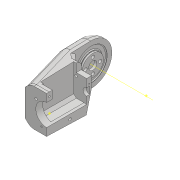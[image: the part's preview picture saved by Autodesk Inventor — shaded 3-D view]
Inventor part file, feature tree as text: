
AUTODESK INVENTOR PART (.ipt)
format: ipt  version: 2018 (Build 220112000, 112)  size: 1,027,584 bytes
history: native  units: mm
features: projected_geometry x49, sketch x47, extrude x39, hole x13, fillet x12, other x10, chamfer x6, reference x3, mirror x1, plane x1
ambient origin geometry x8: Origin, YZ Plane, XZ Plane, XY Plane, X Axis, Y Axis, Z Axis, Center Point
bodies: Solid1 (feature_tree)
feature tree (181):
  extrude  "Extrusion1"  Depth=45.0mm
  extrude  "Extrusion2"  Depth=2.25mm
  hole  "Hole1"  [1 undecoded]
  hole  "Hole2"  [1 undecoded]
  fillet  "Fillet1"  Radius=14.0mm
  extrude  "Extrusion3"  Depth=18.5mm
  extrude  "Extrusion4"  Depth=10.0mm
  extrude  "Extrusion5"  Depth=2.0mm
  extrude  "Extrusion6"  Depth=8.0mm
  hole  "Hole3"  [1 undecoded]
  extrude  "Extrusion7"  Depth=0.5mm
  extrude  "Extrusion8"  Depth=1.0mm TaperAngle=0.0deg
  extrude  "Extrusion9"  Depth=24.5mm
  extrude  "Extrusion10"  Depth=10.0mm
  extrude  "Extrusion11"  Depth=14.5mm
  extrude  "Extrusion13"  Depth=14.5mm
  extrude  "Extrusion14"  Depth=5.0mm
  extrude  "Extrusion15"  Depth=2.25mm
  extrude  "Extrusion16"  Depth=5.0mm
  extrude  "Extrusion17"  Depth=9.0mm
  chamfer  "Chamfer1"  Distance=1.0mm
  fillet  "Fillet7"  Radius=20.7mm
  fillet  "Fillet8"  Radius=32.0mm
  mirror  "Mirror1"
  sketch  "Sketch26"  dims[d55=2.25mm d56=5.0mm]
  extrude  "Extrusion24"  Depth=1.0mm TaperAngle=0.0deg
  extrude  "Extrusion25"  Depth=8.0mm
  extrude  "Extrusion26"  Depth=0.2mm TaperAngle=0.0deg
  extrude  "Extrusion27"  Depth=8.0mm TaperAngle=0.0deg
  other  "Work Axis1"
  plane  "Work Plane2"
  extrude  "Extrusion28"  Depth=0.2mm TaperAngle=0.0deg
  extrude  "Extrusion29"  Depth=2.5mm TaperAngle=45.0deg
  extrude  "Extrusion31"  Depth=0.5mm
  extrude  "Extrusion32"  Depth=36.0mm
  extrude  "Extrusion33"  Depth=60.0mm
  sketch  "Sketch41"  dims[d100=0.2mm d101=0.0mm d102=2.5mm d103=2.0mm d104=45.0deg]
  extrude  "Extrusion34"  Depth=2.3mm
  chamfer  "Chamfer6"  Distance=15.0mm
  fillet  "Fillet9"  Radius=15.0mm
  extrude  "Extrusion35"  Depth=15.0mm TaperAngle=0.0deg
  extrude  "Extrusion36"  Depth=41.5mm
  fillet  "Fillet10"  Radius=15.5mm
  extrude  "Extrusion37"  Depth=5.0mm
  extrude  "Extrusion38"  Depth=100.0mm TaperAngle=0.0deg
  extrude  "Extrusion39"  Depth=11.5mm
  extrude  "Extrusion40"  Depth=11.5mm
  hole  "Hole6"  [1 undecoded]
  fillet  "Fillet12"  Radius=100.0mm
  extrude  "Extrusion41"  Depth=100.0mm TaperAngle=0.0deg
  extrude  "Extrusion42"  Depth=8.0mm
  hole  "Hole7"  [1 undecoded]
  extrude  "Extrusion43"  Depth=1.0mm TaperAngle=0.0deg
  extrude  "Extrusion44"  Depth=2.0mm
  sketch  "Sketch58"  dims[d202=15.0deg d204=10.970628mm]
  hole  "Hole8"  [1 undecoded]
  hole  "Hole9"  [1 undecoded]
  hole  "Hole10"  [1 undecoded]
  hole  "Hole11"  [1 undecoded]
  hole  "Hole12"  [1 undecoded]
  hole  "Hole13"  [1 undecoded]
  hole  "Hole14"  [1 undecoded]
  hole  "Hole15"  [1 undecoded]
  chamfer  "Chamfer10"  Distance=20.5mm
  chamfer  "Chamfer11"  Distance=3.05mm
  chamfer  "Chamfer12"  Distance=14.0mm
  chamfer  "Chamfer13"  Distance=20.5mm
  extrude  "Extrusion45"  Depth=1.55mm TaperAngle=0.0deg
  fillet  "Fillet13"  Radius=8.0mm
  extrude  "Extrusion46"  Depth=2.5mm TaperAngle=0.0deg
  fillet  "Fillet14"  Radius=8.0mm
  fillet  "Fillet15"  Radius=2.5mm
  fillet  "Fillet16"  Radius=4.624622mm
  fillet  "Fillet17"  Radius=4.624622mm
  fillet  "Fillet18"  Radius=2.75mm
  extrude  "Extrusion47"  Depth=2.75mm
  sketch  "Sketch1"  dims[d0=24.5mm d1=45.0mm]
  sketch  "Sketch2"  dims[d2=1.95mm d3=0.0mm d4=2.25mm]
  projected_geometry  "Projected Loop1"
  sketch  "Sketch3"  dims[d5=20.0mm d6=2.25mm]
  projected_geometry  "Projected Loop2"
  sketch  "Sketch4"  dims[d7=5.25mm d8=5.25mm d9=14.0mm]
  projected_geometry  "Projected Loop3"
  sketch  "Sketch5"  dims[d10=5.25mm d11=18.5mm]
  projected_geometry  "Projected Loop4"
  sketch  "Sketch6"  dims[d12=10.0mm d13=0.0mm d14=20.5mm]
  projected_geometry  "Projected Loop5"
  sketch  "Sketch7"  dims[d15=2.0mm d16=2.195mm]
  projected_geometry  "Projected Loop6"
  sketch  "Sketch8"  dims[d17=2.0mm]
  projected_geometry  "Projected Loop7"
  sketch  "Sketch9"  dims[d18=2.4mm d19=6.0mm d20=4.4mm d21=2.0mm d22=90.0deg d23=8.0mm d24=20.594885mm d25=20.5mm]
  projected_geometry  "Projected Loop8"
  projected_geometry  "Projected Loop9"
  sketch  "Sketch10"  dims[d26=26.65mm d27=2.0mm]
  projected_geometry  "Projected Loop10"
  projected_geometry  "Projected Loop11"
  sketch  "Sketch11"  dims[d28=2.0mm]
  projected_geometry  "Projected Loop12"
  sketch  "Sketch12"  dims[d29=2.4mm d30=6.0mm d31=4.4mm d32=2.0mm d33=90.0deg d34=8.0mm d35=20.594885mm d36=0.5mm]
  sketch  "Sketch13"  dims[d37=18.0mm d38=1.0mm d39=0.0mm]
  sketch  "Sketch14"  dims[d41=5.0mm d42=0.0mm d43=24.5mm]
  projected_geometry  "Projected Loop13"
  sketch  "Sketch16"  dims[d44=1.15mm d45=0.0mm d46=10.0mm]
  projected_geometry  "Projected Loop14"
  sketch  "Sketch17"  dims[d47=21.0mm d48=14.5mm]
  projected_geometry  "Projected Loop15"
  sketch  "Sketch18"  dims[d49=20.0mm d50=14.5mm]
  projected_geometry  "Projected Loop16"
  sketch  "Sketch19"  dims[d51=24.5mm d52=5.0mm]
  projected_geometry  "Projected Loop17"
  sketch  "Sketch20"  dims[d53=5.0mm d54=2.25mm]
  projected_geometry  "Projected Loop18"
  projected_geometry  "Projected Loop25"
  sketch  "Sketch31"  dims[d57=5.0mm d58=9.0mm]
  projected_geometry  "Projected Loop30"
  reference  "Reference1"
  sketch  "Sketch32"  dims[d59=14.75mm]
  projected_geometry  "Projected Loop31"
  sketch  "Sketch33"  dims[d60=4.0mm d61=1.0mm d62=0.0mm d63=20.7mm]
  projected_geometry  "Projected Loop32"
  sketch  "Sketch34"  dims[d64=2.3mm d65=6.0mm d66=4.4mm d67=2.0mm d68=90.0deg d69=8.0mm d70=20.594885mm d72=32.0mm]
  projected_geometry  "Projected Loop33"
  other  "Work Point1"
  other  "Work Point2"
  other  "Work Point3"
  sketch  "Sketch35"  dims[d73=3.0mm d74=0.0mm d75=1.0mm d76=0.0mm]
  sketch  "Sketch37"  dims[d77=12.25mm d78=0.0mm d80=8.0mm]
  projected_geometry  "Projected Loop34"
  sketch  "Sketch38"  dims[d81=4.5mm d82=0.0mm d84=0.2mm d85=0.0mm]
  sketch  "Sketch39"  dims[d91=8.0mm d92=0.0mm d93=5.0mm d94=0.0mm]
  sketch  "Sketch40"  dims[d95=5.0mm d96=0.0mm d98=0.2mm d99=0.0mm]
  projected_geometry  "Projected Loop35"
  projected_geometry  "Projected Loop36"
  projected_geometry  "Projected Loop37"
  projected_geometry  "Projected Loop38"
  sketch  "Sketch42"  dims[d105=1.5mm d114=0.5mm]
  projected_geometry  "Projected Loop39"
  sketch  "Sketch43"  dims[d130=60.0mm d131=36.0mm]
  reference  "Reference2"
  reference  "Reference3"
  sketch  "Sketch45"  dims[d146=40.0mm d147=60.0mm]
  projected_geometry  "Projected Loop40"
  sketch  "Sketch46"  dims[d148=0.0mm d149=2.3mm d150=15.0mm d151=0.0mm d152=15.0mm d153=0.0mm]
  projected_geometry  "Projected Loop41"
  sketch  "Sketch48"  dims[d154=15.0mm d155=0.0mm d156=15.0mm d157=0.0mm]
  projected_geometry  "Projected Loop43"
  sketch  "Sketch49"  dims[d158=20.5mm d159=41.5mm d160=15.5mm]
  projected_geometry  "Projected Loop44"
  projected_geometry  "Projected Loop45"
  sketch  "Sketch50"  dims[d161=15.5mm d162=5.0mm]
  projected_geometry  "Projected Loop46"
  sketch  "Sketch52"  dims[d165=100.0mm d166=0.0mm d167=100.0mm d168=0.0mm]
  sketch  "Sketch53"  dims[d172=0.0mm d173=11.5mm]
  projected_geometry  "Projected Loop47"
  sketch  "Sketch54"  dims[d175=11.5mm d176=11.5mm]
  projected_geometry  "Projected Loop48"
  sketch  "Sketch55"  dims[d179=100.0mm d180=0.0mm d187=7.0mm d188=100.0mm d189=0.0mm]
  sketch  "Sketch56"  dims[d193=100.0mm d194=0.0mm d195=100.0mm d196=0.0mm]
  projected_geometry  "Projected Loop49"
  sketch  "Sketch57"  dims[d197=5.0mm d198=2.0mm d199=45.0deg d200=8.0mm]
  projected_geometry  "Projected Loop50"
  projected_geometry  "Projected Loop51"
  projected_geometry  "Projected Loop52"
  projected_geometry  "Projected Loop53"
  projected_geometry  "Projected Loop55"
  projected_geometry  "Projected Loop56"
  projected_geometry  "Projected Loop57"
  sketch  "Sketch59"  dims[d205=15.470628mm d206=1.0mm d207=0.0mm]
  projected_geometry  "Projected Loop58"
  sketch  "Sketch60"  dims[d208=1.0mm d209=0.0mm d213=2.0mm]
  projected_geometry  "Projected Loop59"
  sketch  "Sketch61"  dims[d215=15.0deg d216=4.0mm d217=4.0mm d218=5.0mm d219=0.0mm d222=32.0mm d223=4.0mm d224=0.0mm d225=2.5mm d226=0.0mm d227=6.5mm d228=0.0mm d235=1.567mm d236=15.0mm d237=4.0mm d238=2.0mm d239=90.0deg d240=15.0mm d241=20.594885mm d243=0.75mm d244=20.5mm d245=3.05mm d246=0.0mm d247=14.0mm d248=3.2mm d249=6.0mm d250=4.0mm d251=2.0mm d252=90.0deg d253=8.8mm d254=20.594885mm d255=20.5mm d256=1.55mm d257=0.0mm d258=8.0mm d259=2.5mm d260=0.0mm d261=8.0mm d262=2.5mm d263=0.0mm d266=4.624622mm d267=4.624622mm d268=2.75mm d269=2.75mm d270=2.35mm d271=2.35mm d272=14.0mm d273=4.0mm d274=5.6mm d275=3.708mm d276=3.023mm d277=2.0mm d278=14.3117mm d279=17.0mm d280=0.0mm d281=4.0mm d282=3.708mm d283=3.023mm d284=2.0mm d285=14.3117mm d286=19.0mm d287=0.0mm d288=4.0mm d289=3.708mm d290=3.023mm d291=2.0mm d292=14.3117mm d293=20.0mm d294=0.0mm d295=2.3mm d296=4.0mm d297=4.4mm d298=2.0mm d299=90.0deg d300=32.25mm d301=0.0mm d302=3.3mm d303=4.0mm d304=6.3mm d305=2.0mm d306=90.0deg d307=32.25mm d308=0.0mm d309=1.567mm d310=4.0mm d311=6.3mm d312=2.0mm d313=90.0deg d314=45.0mm d315=20.594885mm d316=1.567mm d317=4.0mm d318=6.3mm d319=2.0mm d320=90.0deg d321=55.0mm d322=20.594885mm d323=2.459mm d324=6.0mm d325=6.3mm d326=2.0mm d327=90.0deg d328=50.0mm d329=20.594885mm d330=3.0mm d331=2.0mm d332=45.0deg d333=5.0mm d334=20.0mm d335=45.0deg d336=5.0mm d337=20.0mm d338=45.0deg d339=5.0mm d340=20.0mm d341=45.0deg d342=6.0mm d343=6.0mm d344=6.0mm d345=6.0mm d346=2.0mm d347=0.0mm d348=1.5mm d349=6.0mm d350=6.0mm d351=6.0mm d352=6.0mm d353=3.0mm d354=0.0mm d355=1.5mm d356=0.4mm d357=0.4mm d358=0.3mm d359=1.0mm d360=0.6mm d361=32.25mm d362=0.0mm]
  parser-record x1  (decoder bookkeeping rows leaked as tree rows — omitted from the tree; the rows remain in map.json)
  other  "servocheck.iam"
  other  "LX-16A:3"
  other  "DUOPAN-SG-SJ_10"
  projected_geometry  "Project Cut Edges1"
  projected_geometry  "Project Cut Edges3"
  other  "bottomarm:1"
  other  "arm1:1"
note: 13 required parameter values undecoded (feature->parameter linkage not recoverable at this tier; creation-order binding heuristic only, values carry confidence <= 0.55)
note: 1 file-system path scrubbed to <path> (originals preserved in map.json)
